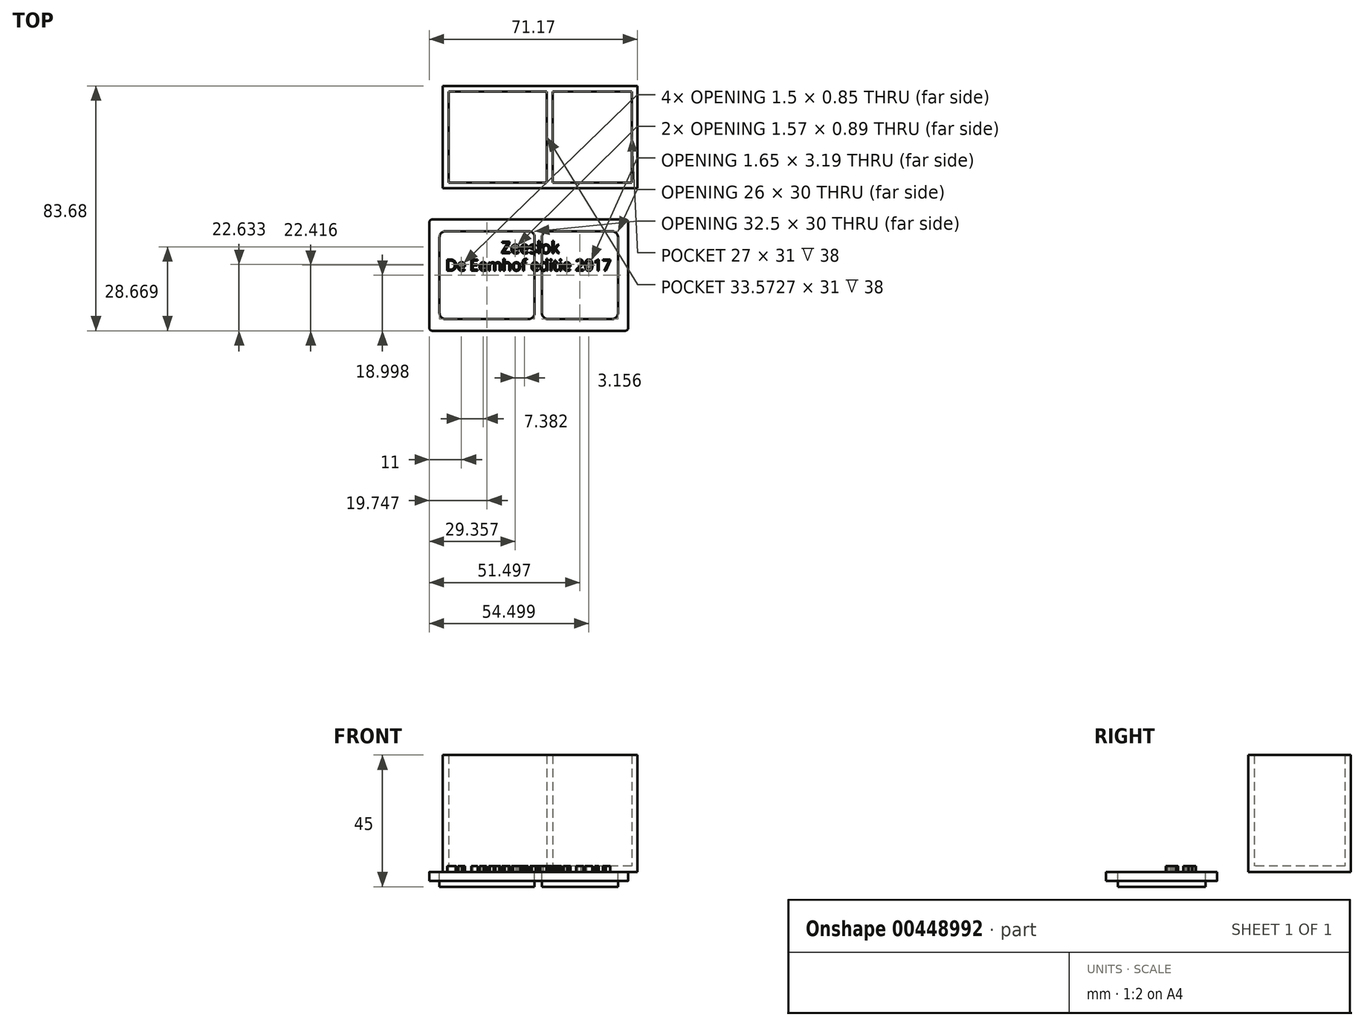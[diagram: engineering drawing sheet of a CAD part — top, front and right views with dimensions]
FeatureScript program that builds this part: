
annotation { "Feature Type Name" : "Feature", "Feature Type Description" : "" }
export const myFeature = defineFeature(function(context is Context, id is Id, definition is map)
    precondition{}
    {
        {
            var Q0;
            Q0=qCreatedBy(makeId("Top.planeOp"),FACE);
            var sketch = newSketch(context, id + "F0", { "sketchPlane" : qUnion([Q0])});
            skSolve(sketch);
        }
        {
            var Q0;
            Q0=qCreatedBy(makeId("Top.planeOp"),FACE);
            var sketch = newSketch(context, id + "F1", { "sketchPlane" : qUnion([Q0])});
            skLineSegment(sketch, "E0", {"start": v(-45.99, -17.17) * mm, "end": v(20.58, -17.17) * mm});
            skLineSegment(sketch, "E1", {"start": v(20.58, -17.17) * mm, "end": v(20.58, 17.83) * mm});
            skLineSegment(sketch, "E2", {"start": v(20.58, 17.83) * mm, "end": v(-45.99, 17.83) * mm});
            skLineSegment(sketch, "E3", {"start": v(-45.99, 17.83) * mm, "end": v(-45.99, -17.17) * mm});
            skLineSegment(sketch, "E4.0", {"start": v(-43.99, 15.83) * mm, "end": v(-43.99, -15.17) * mm});
            skLineSegment(sketch, "E5.0", {"start": v(18.58, 15.83) * mm, "end": v(-8.42, 15.83) * mm});
            skLineSegment(sketch, "E6.0", {"start": v(-43.99, -15.17) * mm, "end": v(-10.42, -15.17) * mm});
            skLineSegment(sketch, "E7.0", {"start": v(18.58, -15.17) * mm, "end": v(18.58, 15.83) * mm});
            skLineSegment(sketch, "E8.0", {"start": v(-8.42, -15.17) * mm, "end": v(-8.42, 15.83) * mm});
            skLineSegment(sketch, "E9.0", {"start": v(-10.42, -15.17) * mm, "end": v(-10.42, 15.83) * mm});
            skLineSegment(sketch, "E10.trimOffspring", {"start": v(-10.42, 15.83) * mm, "end": v(-43.99, 15.83) * mm});
            skLineSegment(sketch, "E11.trimOffspring", {"start": v(-8.42, -15.17) * mm, "end": v(18.58, -15.17) * mm});
            skSolve(sketch);
        }
        {
            var Q0;
            Q0 = qSketchRegion(id + "F1", true);
            extrude(context, id + "F2", {"entities" : qUnion([Q0]), "depth" : 40 * mm});
        }
        {
            var Q0;
            Q0 = qSketchRegion(id + "F0", true);
            var Q1;
            Q1=makeQuery(id+"F1.imprint","IMPRINT",FACE,{"disambiguationData":[TD([[makeQuery(id+"F1.imprint","IMPRINT",EDGE,{"derivedFrom":sQuery(id+"F1.wireOp",EDGE,"E5.0")}),1.0]])]});
            extrude(context, id + "F3", {"entities" : qUnion([Q0, Q1]), "operationType" : NewBodyOperationType.ADD, "depth" : 2 * mm});
        }
        {
            var Q0;
            Q0=makeQuery(id+"F1.imprint","IMPRINT",FACE,{"disambiguationData":[TD([[makeQuery(id+"F1.imprint","IMPRINT",EDGE,{"derivedFrom":sQuery(id+"F1.wireOp",EDGE,"E4.0")}),1.0]])]});
            extrude(context, id + "F4", {"entities" : qUnion([Q0]), "operationType" : NewBodyOperationType.ADD, "depth" : 2 * mm});
        }
        {
            var Q0;
            Q0=qCreatedBy(makeId("Top.planeOp"),FACE);
            var sketch = newSketch(context, id + "F5", { "sketchPlane" : qUnion([Q0])});
            skLineSegment(sketch, "E12", {"start": v(-45.1, -31.85) * mm, "end": v(-16.6, -31.85) * mm});
            skLineSegment(sketch, "E13", {"start": v(-14.6, -33.85) * mm, "end": v(-14.6, -59.85) * mm});
            skLineSegment(sketch, "E14", {"start": v(-16.6, -61.85) * mm, "end": v(-45.1, -61.85) * mm});
            skLineSegment(sketch, "E15", {"start": v(-47.1, -59.85) * mm, "end": v(-47.1, -33.85) * mm});
            skLineSegment(sketch, "E16.0", {"start": v(-12.1, -33.85) * mm, "end": v(-12.1, -59.85) * mm});
            skLineSegment(sketch, "E17.0", {"start": v(13.9, -33.85) * mm, "end": v(13.9, -59.85) * mm});
            skLineSegment(sketch, "E18", {"start": v(-10.1, -31.85) * mm, "end": v(11.9, -31.85) * mm});
            skLineSegment(sketch, "E19", {"start": v(11.9, -61.85) * mm, "end": v(-10.1, -61.85) * mm});
            skLineSegment(sketch, "E20", {"start": v(-50.6, -28.85) * mm, "end": v(-50.6, -64.85) * mm});
            skLineSegment(sketch, "E21", {"start": v(17.4, -28.85) * mm, "end": v(17.4, -64.85) * mm});
            skLineSegment(sketch, "E22", {"start": v(16.4, -27.85) * mm, "end": v(-49.6, -27.85) * mm});
            skLineSegment(sketch, "E23", {"start": v(-49.6, -65.85) * mm, "end": v(16.4, -65.85) * mm});
            skPoint(sketch, "E24.visualSharp", {"position": v(-47.1, -31.85) * mm});
            skArc(sketch, "E24.filletArc", {"start": v(-45.1, -31.85) * mm, "mid": v(-46.5, -32.44) * mm, "end": v(-47.1, -33.85) * mm});
            skPoint(sketch, "E25.visualSharp", {"position": v(-14.6, -31.85) * mm});
            skArc(sketch, "E25.filletArc", {"start": v(-14.6, -33.85) * mm, "mid": v(-15.18, -32.44) * mm, "end": v(-16.6, -31.85) * mm});
            skPoint(sketch, "E26.visualSharp", {"position": v(-12.1, -31.85) * mm});
            skArc(sketch, "E26.filletArc", {"start": v(-10.1, -31.85) * mm, "mid": v(-11.5, -32.44) * mm, "end": v(-12.1, -33.85) * mm});
            skPoint(sketch, "E27.visualSharp", {"position": v(13.9, -31.85) * mm});
            skArc(sketch, "E27.filletArc", {"start": v(13.9, -33.85) * mm, "mid": v(13.32, -32.44) * mm, "end": v(11.9, -31.85) * mm});
            skPoint(sketch, "E28.visualSharp", {"position": v(13.9, -61.85) * mm});
            skArc(sketch, "E28.filletArc", {"start": v(11.9, -61.85) * mm, "mid": v(13.32, -61.27) * mm, "end": v(13.9, -59.85) * mm});
            skPoint(sketch, "E29.visualSharp", {"position": v(-12.1, -61.85) * mm});
            skArc(sketch, "E29.filletArc", {"start": v(-12.1, -59.85) * mm, "mid": v(-11.5, -61.27) * mm, "end": v(-10.1, -61.85) * mm});
            skPoint(sketch, "E30.visualSharp", {"position": v(-14.6, -61.85) * mm});
            skArc(sketch, "E30.filletArc", {"start": v(-16.6, -61.85) * mm, "mid": v(-15.18, -61.27) * mm, "end": v(-14.6, -59.85) * mm});
            skPoint(sketch, "E31.visualSharp", {"position": v(-47.1, -61.85) * mm});
            skArc(sketch, "E31.filletArc", {"start": v(-47.1, -59.85) * mm, "mid": v(-46.5, -61.27) * mm, "end": v(-45.1, -61.85) * mm});
            skPoint(sketch, "E32.visualSharp", {"position": v(-50.6, -27.85) * mm});
            skArc(sketch, "E32.filletArc", {"start": v(-49.6, -27.85) * mm, "mid": v(-50.3, -28.14) * mm, "end": v(-50.6, -28.85) * mm});
            skPoint(sketch, "E33.visualSharp", {"position": v(17.4, -27.85) * mm});
            skArc(sketch, "E33.filletArc", {"start": v(17.4, -28.85) * mm, "mid": v(17.11, -28.14) * mm, "end": v(16.4, -27.85) * mm});
            skPoint(sketch, "E34.visualSharp", {"position": v(17.4, -65.85) * mm});
            skArc(sketch, "E34.filletArc", {"start": v(16.4, -65.85) * mm, "mid": v(17.11, -65.56) * mm, "end": v(17.4, -64.85) * mm});
            skPoint(sketch, "E35.visualSharp", {"position": v(-50.6, -65.85) * mm});
            skArc(sketch, "E35.filletArc", {"start": v(-50.6, -64.85) * mm, "mid": v(-50.3, -65.56) * mm, "end": v(-49.6, -65.85) * mm});
            skSolve(sketch);
        }
        {
            var Q0;
            Q0=makeQuery(id+"F5.imprint","IMPRINT",FACE,{"disambiguationData":[TD([[makeQuery(id+"F5.imprint","IMPRINT",EDGE,{"derivedFrom":sQuery(id+"F5.wireOp",EDGE,"E16.0")}),1.0]])]});
            var Q1;
            Q1=makeQuery(id+"F5.imprint","IMPRINT",FACE,{"disambiguationData":[TD([[makeQuery(id+"F5.imprint","IMPRINT",EDGE,{"derivedFrom":sQuery(id+"F5.wireOp",EDGE,"E12")}),-1.0]])]});
            extrude(context, id + "F6", {"entities" : qUnion([Q0, Q1]), "depth" : -5 * mm});
        }
        {
            var Q0;
            Q0=makeQuery(id+"F5.imprint","IMPRINT",FACE,{"disambiguationData":[TD([[makeQuery(id+"F5.imprint","IMPRINT",EDGE,{"derivedFrom":sQuery(id+"F5.wireOp",EDGE,"E12")}),1.0]])]});
            extrude(context, id + "F7", {"entities" : qUnion([Q0]), "depth" : -3 * mm});
        }
        {
            var Q0;
            Q0=qCreatedBy(makeId("Top.planeOp"),FACE);
            var sketch = newSketch(context, id + "F8", { "sketchPlane" : qUnion([Q0])});
            skText(sketch, "E36", { "text": "Zeeslok ", "fontName": "OpenSans-Regular.ttf"});
            skText(sketch, "E37", { "text": "De Eemhof editie 2017", "fontName": "OpenSans-Regular.ttf"});
            const initialGuessF8  = {"E36": [-0.02603, -0.03942, 1, 0, 0.00405], "E37": [-0.04501, -0.04535, 1, 0, 0.00386]};
            skSetInitialGuess(sketch, initialGuessF8);
            skSolve(sketch);
        }
        {
            var Q0;
            Q0 = qSketchRegion(id + "F8", true);
            extrude(context, id + "F9", {"entities" : qUnion([Q0]), "depth" : 2 * mm});
        }
    });
